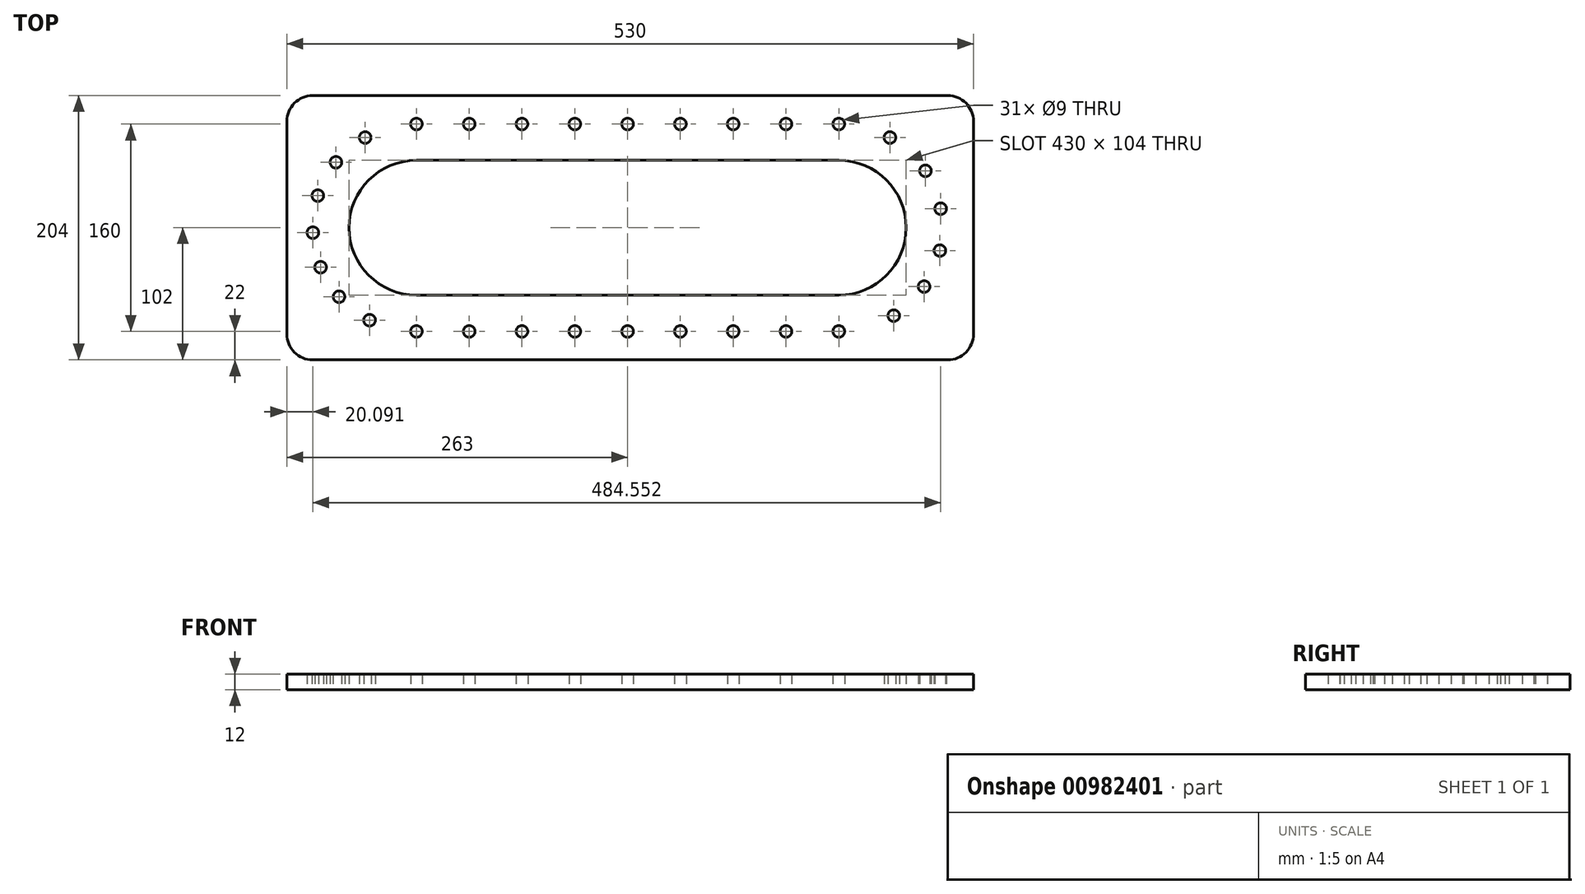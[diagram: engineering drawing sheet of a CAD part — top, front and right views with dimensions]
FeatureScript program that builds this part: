
annotation { "Feature Type Name" : "Feature", "Feature Type Description" : "" }
export const myFeature = defineFeature(function(context is Context, id is Id, definition is map)
    precondition{}
    {
        {
            var Q0;
            Q0=qCreatedBy(makeId("Top.planeOp"),FACE);
            var sketch = newSketch(context, id + "F0", { "sketchPlane" : qUnion([Q0])});
            skLineSegment(sketch, "E0.bottom", {"start": v(-20, 0) * mm, "end": v(-510, 0) * mm});
            skLineSegment(sketch, "E0.top", {"start": v(-20, -204) * mm, "end": v(-510, -204) * mm});
            skLineSegment(sketch, "E0.left", {"start": v(0, -20) * mm, "end": v(0, -184) * mm});
            skLineSegment(sketch, "E0.right", {"start": v(-530, -20) * mm, "end": v(-530, -184) * mm});
            skLineSegment(sketch, "E1.bottom", {"start": v(-430, -50) * mm, "end": v(-104, -50) * mm});
            skLineSegment(sketch, "E1.top", {"start": v(-430, -154) * mm, "end": v(-104, -154) * mm});
            skPoint(sketch, "E2", {"position": v(-430, -102) * mm});
            skPoint(sketch, "E3", {"position": v(-104, -102) * mm});
            skArc(sketch, "E4", {"start": v(-430, -50) * mm, "mid": v(-482, -102) * mm, "end": v(-430, -154) * mm});
            skArc(sketch, "E5", {"start": v(-104, -154) * mm, "mid": v(-52, -102) * mm, "end": v(-104, -50) * mm});
            skArc(sketch, "E6", {"start": v(-104, -182) * mm, "mid": v(-24, -102) * mm, "end": v(-104, -22) * mm});
            skArc(sketch, "E7", {"start": v(-430, -22) * mm, "mid": v(-510, -102) * mm, "end": v(-430, -182) * mm});
            skPoint(sketch, "E8.visualSharp", {"position": v(-530, -204) * mm});
            skArc(sketch, "E8.filletArc", {"start": v(-530, -184) * mm, "mid": v(-524.14, -198.14) * mm, "end": v(-510, -204) * mm});
            skPoint(sketch, "E9.visualSharp", {"position": v(0, -204) * mm});
            skArc(sketch, "E9.filletArc", {"start": v(-20, -204) * mm, "mid": v(-5.86, -198.14) * mm, "end": v(0, -184) * mm});
            skPoint(sketch, "E10.visualSharp", {"position": v(0, 0) * mm});
            skArc(sketch, "E10.filletArc", {"start": v(0, -20) * mm, "mid": v(-5.86, -5.86) * mm, "end": v(-20, 0) * mm});
            skPoint(sketch, "E11.visualSharp", {"position": v(-530, 0) * mm});
            skArc(sketch, "E11.filletArc", {"start": v(-510, 0) * mm, "mid": v(-524.14, -5.86) * mm, "end": v(-530, -20) * mm});
            skLineSegment(sketch, "E12", {"start": v(-104, -182) * mm, "end": v(-430, -182) * mm});
            skLineSegment(sketch, "E13", {"start": v(-430, -22) * mm, "end": v(-104, -22) * mm});
            skCircle(sketch, "E14", {"center": v(-430, -22) * mm, "radius": 4.5 * mm});
            skCircle(sketch, "E15", {"center": v(-430, -182) * mm, "radius": 4.5 * mm});
            skCircle(sketch, "E16", {"center": v(-104, -182) * mm, "radius": 4.5 * mm});
            skCircle(sketch, "E17", {"center": v(-389.25, -22) * mm, "radius": 4.5 * mm});
            skCircle(sketch, "E18", {"center": v(-348.5, -22) * mm, "radius": 4.5 * mm});
            skCircle(sketch, "E19", {"center": v(-307.75, -22) * mm, "radius": 4.5 * mm});
            skCircle(sketch, "E20", {"center": v(-267, -22) * mm, "radius": 4.5 * mm});
            skCircle(sketch, "E21", {"center": v(-226.25, -22) * mm, "radius": 4.5 * mm});
            skCircle(sketch, "E22", {"center": v(-185.5, -22) * mm, "radius": 4.5 * mm});
            skCircle(sketch, "E23", {"center": v(-104, -22) * mm, "radius": 4.5 * mm});
            skCircle(sketch, "E24", {"center": v(-144.75, -22) * mm, "radius": 4.5 * mm});
            skCircle(sketch, "E25", {"center": v(-389.25, -182) * mm, "radius": 4.5 * mm});
            skCircle(sketch, "E26", {"center": v(-348.5, -182) * mm, "radius": 4.5 * mm});
            skCircle(sketch, "E27", {"center": v(-307.75, -182) * mm, "radius": 4.5 * mm});
            skCircle(sketch, "E28", {"center": v(-267, -182) * mm, "radius": 4.5 * mm});
            skCircle(sketch, "E29", {"center": v(-226.25, -182) * mm, "radius": 4.5 * mm});
            skCircle(sketch, "E30", {"center": v(-185.5, -182) * mm, "radius": 4.5 * mm});
            skCircle(sketch, "E31", {"center": v(-144.75, -182) * mm, "radius": 4.5 * mm});
            skCircle(sketch, "E32", {"center": v(-61.57, -169.82) * mm, "radius": 4.5 * mm});
            skCircle(sketch, "E33", {"center": v(-38.2, -147.49) * mm, "radius": 4.5 * mm});
            skCircle(sketch, "E34", {"center": v(-25.97, -119.63) * mm, "radius": 4.5 * mm});
            skCircle(sketch, "E35", {"center": v(-25.36, -87.33) * mm, "radius": 4.5 * mm});
            skCircle(sketch, "E36", {"center": v(-37.1, -58.14) * mm, "radius": 4.5 * mm});
            skCircle(sketch, "E37", {"center": v(-64.5, -32.43) * mm, "radius": 4.5 * mm});
            skCircle(sketch, "E38", {"center": v(-469.5, -32.43) * mm, "radius": 4.5 * mm});
            skCircle(sketch, "E39", {"center": v(-492.06, -51.51) * mm, "radius": 4.5 * mm});
            skCircle(sketch, "E40", {"center": v(-506.08, -77.27) * mm, "radius": 4.5 * mm});
            skCircle(sketch, "E41", {"center": v(-509.9, -105.82) * mm, "radius": 4.5 * mm});
            skCircle(sketch, "E42", {"center": v(-503.95, -132.51) * mm, "radius": 4.5 * mm});
            skCircle(sketch, "E43", {"center": v(-466.12, -173.38) * mm, "radius": 4.5 * mm});
            skCircle(sketch, "E44", {"center": v(-489.72, -155.23) * mm, "radius": 4.5 * mm});
            skSolve(sketch);
        }
        {
            var Q0;
            Q0=makeQuery(id+"F0.imprint","IMPRINT",FACE,{"disambiguationData":[TD([[makeQuery(id+"F0.imprint","IMPRINT",EDGE,{"derivedFrom":sQuery(id+"F0.wireOp",EDGE,"E0.bottom")}),1.0]])]});
            var Q1;
            Q1=makeQuery(id+"F0.imprint","IMPRINT",FACE,{"disambiguationData":[TD([[makeQuery(id+"F0.imprint","IMPRINT",EDGE,{"derivedFrom":sQuery(id+"F0.wireOp",EDGE,"E1.bottom")}),1.0]])]});
            extrude(context, id + "F1", {"entities" : qUnion([Q0, Q1]), "depth" : 12 * mm, "offsetDistance" : 25 * mm});
        }
    });
